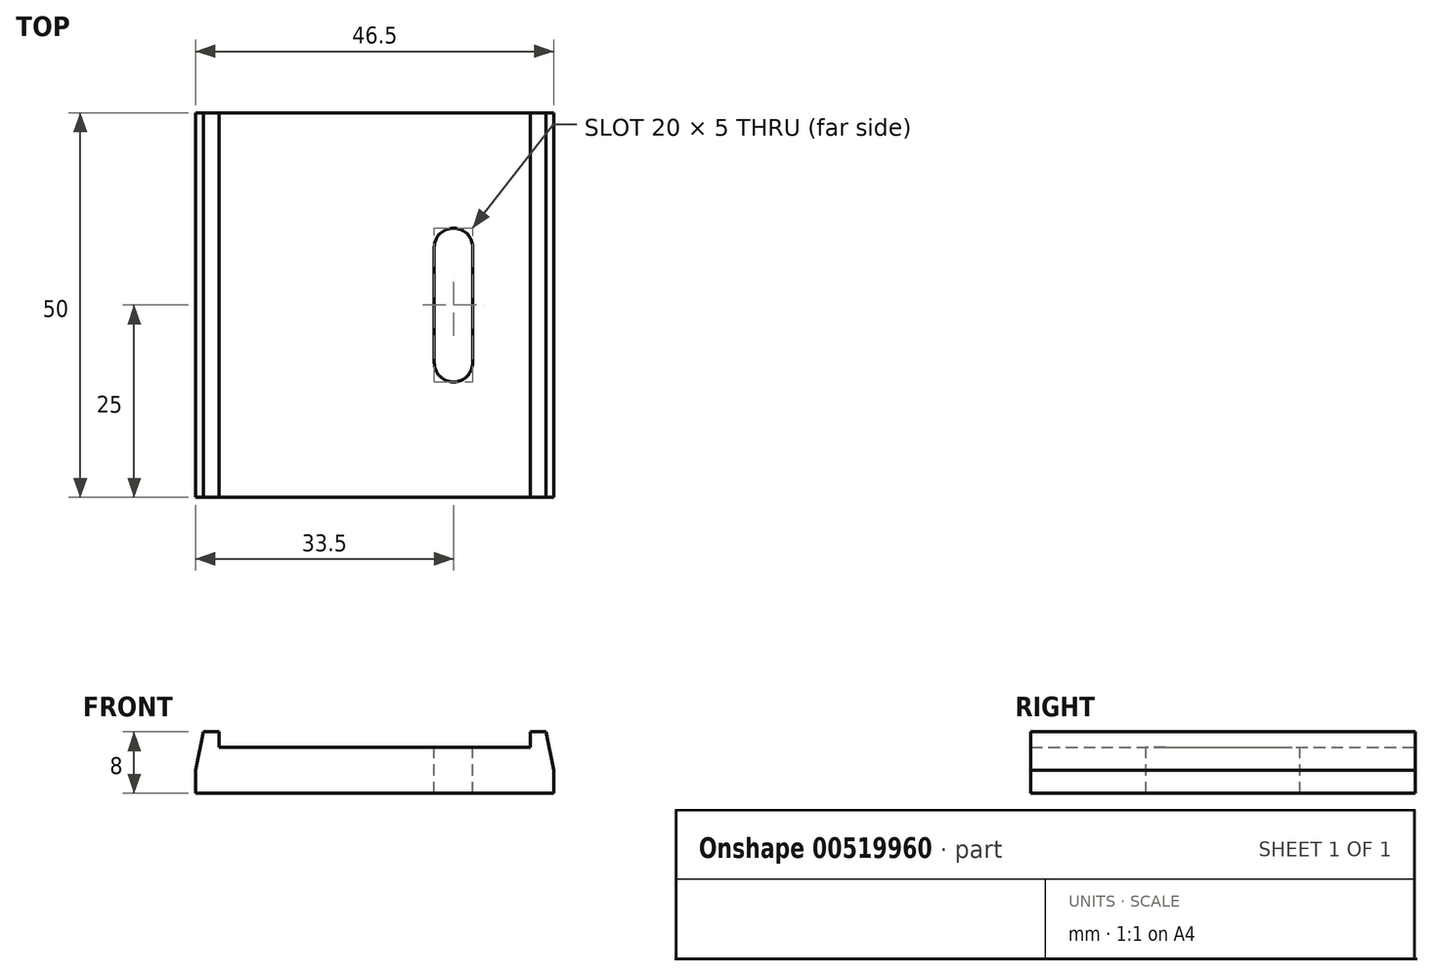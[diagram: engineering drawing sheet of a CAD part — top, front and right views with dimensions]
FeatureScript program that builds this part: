
annotation { "Feature Type Name" : "Feature", "Feature Type Description" : "" }
export const myFeature = defineFeature(function(context is Context, id is Id, definition is map)
    precondition{}
    {
        {
            var Q0;
            Q0=qCreatedBy(makeId("Front.planeOp"),FACE);
            var sketch = newSketch(context, id + "F0", { "sketchPlane" : qUnion([Q0])});
            skLineSegment(sketch, "E0.bottom", {"start": v(0, 0) * mm, "end": v(40.5, 0) * mm});
            skLineSegment(sketch, "E0.top", {"start": v(0, -6) * mm, "end": v(40.5, -6) * mm});
            skLineSegment(sketch, "E1.bottom", {"start": v(0, -6) * mm, "end": v(-3, -6) * mm});
            skLineSegment(sketch, "E1.top", {"start": v(0, 2) * mm, "end": v(-3, 2) * mm});
            skLineSegment(sketch, "E1.left", {"start": v(0, 0) * mm, "end": v(0, 2) * mm});
            skLineSegment(sketch, "E1.right", {"start": v(-3, -6) * mm, "end": v(-3, 2) * mm});
            skLineSegment(sketch, "E2.bottom", {"start": v(40.5, -6) * mm, "end": v(43.5, -6) * mm});
            skLineSegment(sketch, "E2.top", {"start": v(40.5, 2) * mm, "end": v(43.5, 2) * mm});
            skLineSegment(sketch, "E2.left", {"start": v(40.5, 0) * mm, "end": v(40.5, 2) * mm});
            skLineSegment(sketch, "E2.right", {"start": v(43.5, -6) * mm, "end": v(43.5, 2) * mm});
            skSolve(sketch);
        }
        {
            var Q0;
            Q0=makeQuery(id+"F0.imprint","IMPRINT",FACE,{"disambiguationData":[TD([[makeQuery(id+"F0.imprint","IMPRINT",EDGE,{"derivedFrom":sQuery(id+"F0.wireOp",EDGE,"E0.bottom")}),-1.0]])]});
            extrude(context, id + "F1", {"entities" : qUnion([Q0]), "depth" : 50 * mm, "offsetDistance" : 25 * mm});
        }
        {
            var Q0;
            Q0=makeQuery(id+"F1.opExtrude","SWEPT_EDGE",EDGE,{"disambiguationData":[OSD([sQuery(id+"F0.wireOp",EDGE,"E1.top"),sQuery(id+"F0.wireOp",EDGE,"E1.right")])]});
            chamfer(context, id + "F2", {"entities" : qUnion([Q0]), "chamferType" : ChamferType.TWO_OFFSETS, "width1" : 5 * mm, "oppositeDirection" : false, "width2" : 1 * mm, "tangentPropagation" : true});
        }
        {
            var Q0;
            Q0=makeQuery(id+"F1.opExtrude","SWEPT_EDGE",EDGE,{"disambiguationData":[OSD([sQuery(id+"F0.wireOp",EDGE,"E2.top"),sQuery(id+"F0.wireOp",EDGE,"E2.right")])]});
            chamfer(context, id + "F3", {"entities" : qUnion([Q0]), "chamferType" : ChamferType.TWO_OFFSETS, "width1" : 1 * mm, "oppositeDirection" : false, "width2" : 5 * mm, "tangentPropagation" : true});
        }
        {
            var Q0;
            Q0=makeQuery(id+"F1.opExtrude","SWEPT_FACE",FACE,{"disambiguationData":[OSD([sQuery(id+"F0.wireOp",EDGE,"E0.bottom")])]});
            var sketch = newSketch(context, id + "F4", { "sketchPlane" : qUnion([Q0])});
            skLineSegment(sketch, "E3.bottom", {"start": v(30.5, -35) * mm, "end": v(30.5, -35) * mm});
            skLineSegment(sketch, "E3.top", {"start": v(30.5, -15) * mm, "end": v(30.5, -15) * mm});
            skLineSegment(sketch, "E3.left", {"start": v(33, -32.5) * mm, "end": v(33, -17.5) * mm});
            skLineSegment(sketch, "E3.right", {"start": v(28, -32.5) * mm, "end": v(28, -17.5) * mm});
            skLineSegment(sketch, "E4", {"start": v(30.5, -15) * mm, "end": v(30.5, -35) * mm, "construction": true});
            skPoint(sketch, "E5.visualSharp", {"position": v(28, -15) * mm});
            skArc(sketch, "E5.filletArc", {"start": v(30.5, -15) * mm, "mid": v(28.73, -15.73) * mm, "end": v(28, -17.5) * mm});
            skPoint(sketch, "E6.visualSharp", {"position": v(33, -15) * mm});
            skArc(sketch, "E6.filletArc", {"start": v(33, -17.5) * mm, "mid": v(32.27, -15.73) * mm, "end": v(30.5, -15) * mm});
            skPoint(sketch, "E7.visualSharp", {"position": v(33, -35) * mm});
            skArc(sketch, "E7.filletArc", {"start": v(30.5, -35) * mm, "mid": v(32.27, -34.27) * mm, "end": v(33, -32.5) * mm});
            skPoint(sketch, "E8.visualSharp", {"position": v(28, -35) * mm});
            skArc(sketch, "E8.filletArc", {"start": v(28, -32.5) * mm, "mid": v(28.73, -34.27) * mm, "end": v(30.5, -35) * mm});
            skLineSegment(sketch, "E9", {"start": v(28, -25) * mm, "end": v(33, -25) * mm, "construction": true});
            skSolve(sketch);
        }
        {
            var Q0;
            Q0=makeQuery(id+"F4.imprint","IMPRINT",FACE,{"disambiguationData":[TD([[makeQuery(id+"F4.imprint","IMPRINT",EDGE,{"derivedFrom":sQuery(id+"F4.wireOp",EDGE,"E3.left")}),1.0]])]});
            extrude(context, id + "F5", {"entities" : qUnion([Q0]), "operationType" : NewBodyOperationType.REMOVE, "oppositeDirection" : true, "depth" : 25 * mm, "offsetDistance" : 25 * mm});
        }
    });
